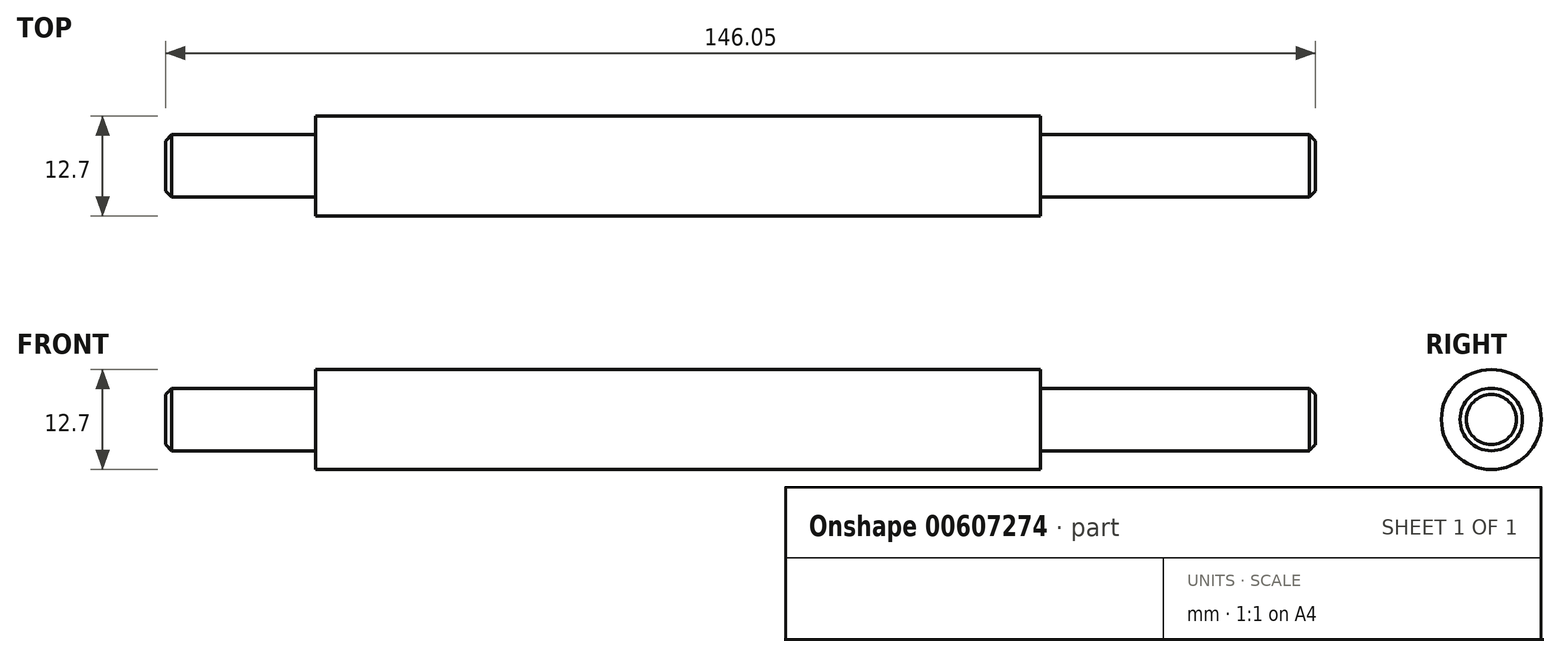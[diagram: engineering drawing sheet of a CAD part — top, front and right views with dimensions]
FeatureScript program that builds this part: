
annotation { "Feature Type Name" : "Feature", "Feature Type Description" : "" }
export const myFeature = defineFeature(function(context is Context, id is Id, definition is map)
    precondition{}
    {
        {
            var Q0;
            Q0=qCreatedBy(makeId("Front.planeOp"),FACE);
            var sketch = newSketch(context, id + "F0", { "sketchPlane" : qUnion([Q0])});
            skLineSegment(sketch, "E0", {"start": v(0, 0) * mm, "end": v(146.05, 0) * mm});
            skLineSegment(sketch, "E1", {"start": v(146.05, 0) * mm, "end": v(111.12, 0) * mm});
            skLineSegment(sketch, "E2", {"start": v(111.12, 0) * mm, "end": v(111.12, 6.35) * mm});
            skLineSegment(sketch, "E3", {"start": v(111.12, 6.35) * mm, "end": v(19.05, 6.35) * mm});
            skLineSegment(sketch, "E4", {"start": v(19.05, 6.35) * mm, "end": v(19.05, 0) * mm});
            skLineSegment(sketch, "E5", {"start": v(19.05, 0) * mm, "end": v(0, 0) * mm});
            skLineSegment(sketch, "E6", {"start": v(0, 0) * mm, "end": v(0, 3.97) * mm});
            skLineSegment(sketch, "E7", {"start": v(0, 3.97) * mm, "end": v(19.05, 3.97) * mm});
            skLineSegment(sketch, "E8", {"start": v(19.05, 3.97) * mm, "end": v(146.05, 3.97) * mm});
            skLineSegment(sketch, "E9", {"start": v(146.05, 3.97) * mm, "end": v(146.05, 0) * mm});
            skSolve(sketch);
        }
        {
            var Q0;
            Q0 = qSketchRegion(id + "F0", true);
            var Q1;
            Q1=sQuery(id+"F0.wireOp",EDGE,"E0");
            revolve(context, id + "F1", {"entities" : qUnion([Q0]), "axis" : qUnion([Q1]), "revolveType" : RevolveType.FULL});
        }
        {
            var Q0;
            Q0=makeQuery(id+"F1.opRevolve","SWEPT_EDGE",EDGE,{"disambiguationData":[OSD([sQuery(id+"F0.wireOp",EDGE,"E8"),sQuery(id+"F0.wireOp",EDGE,"E9")])]});
            var Q1;
            Q1=makeQuery(id+"F1.opRevolve","SWEPT_EDGE",EDGE,{"disambiguationData":[OSD([sQuery(id+"F0.wireOp",EDGE,"E6"),sQuery(id+"F0.wireOp",EDGE,"E7")])]});
            chamfer(context, id + "F2", {"entities" : qUnion([Q0, Q1]), "width" : 0.79 * mm, "tangentPropagation" : true});
        }
    });
